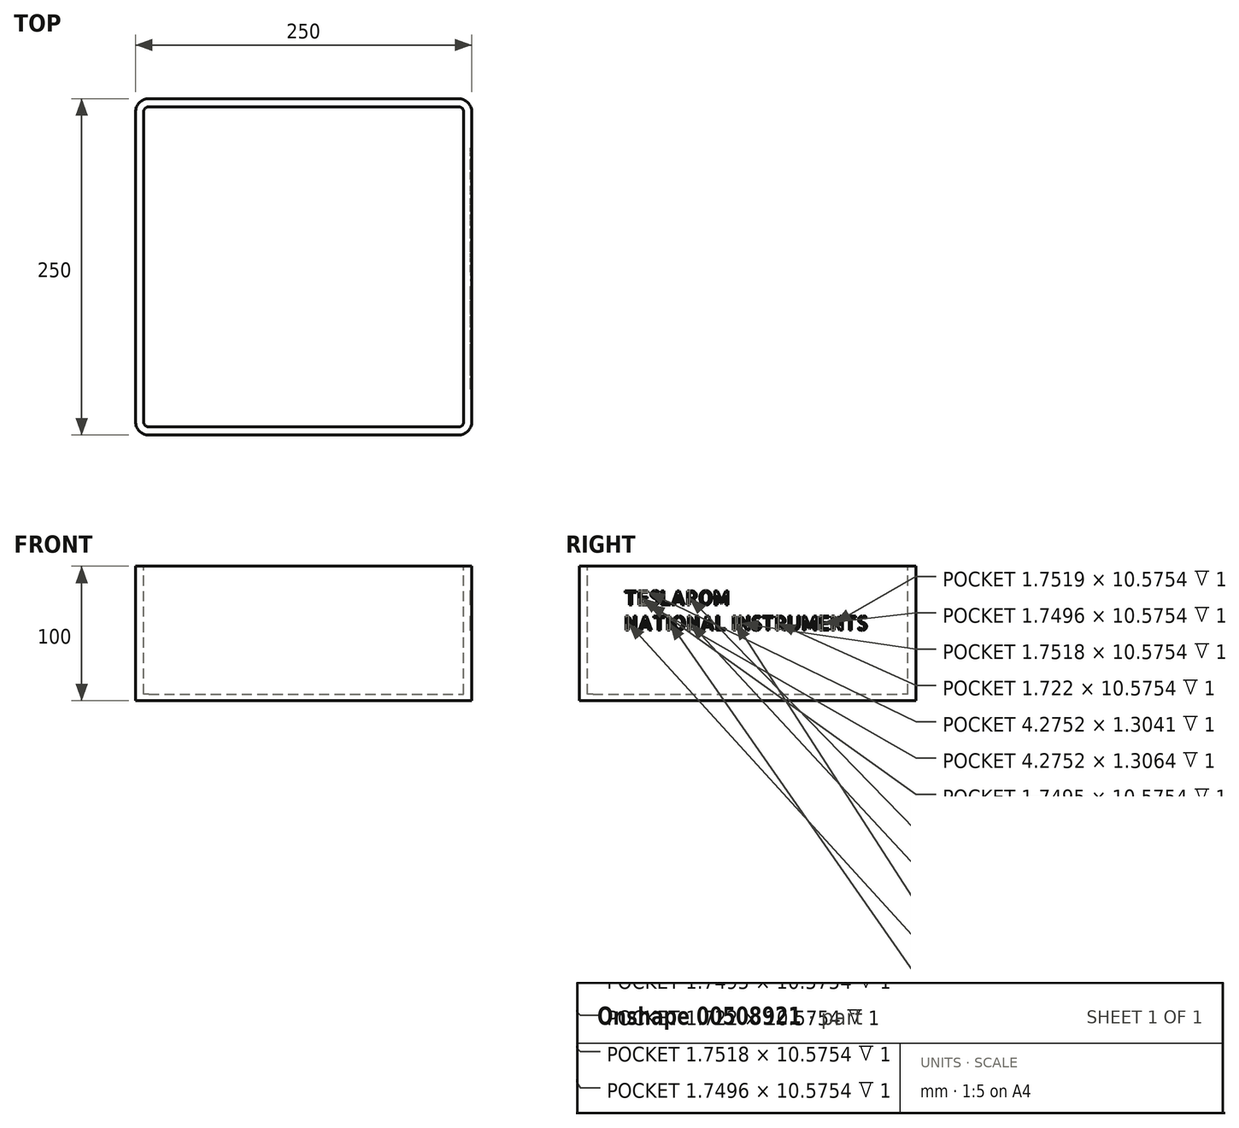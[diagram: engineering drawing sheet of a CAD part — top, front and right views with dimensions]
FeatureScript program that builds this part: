
annotation { "Feature Type Name" : "Feature", "Feature Type Description" : "" }
export const myFeature = defineFeature(function(context is Context, id is Id, definition is map)
    precondition{}
    {
        {
            var Q0;
            Q0=qCreatedBy(makeId("Top.planeOp"),FACE);
            var sketch = newSketch(context, id + "F0", { "sketchPlane" : qUnion([Q0])});
            skLineSegment(sketch, "E0.bottom", {"start": v(10, 0) * mm, "end": v(240, 0) * mm});
            skLineSegment(sketch, "E0.top", {"start": v(10, 250) * mm, "end": v(240, 250) * mm});
            skLineSegment(sketch, "E0.left", {"start": v(0, 10) * mm, "end": v(0, 240) * mm});
            skLineSegment(sketch, "E0.right", {"start": v(250, 10) * mm, "end": v(250, 240) * mm});
            skPoint(sketch, "E1.visualSharp", {"position": v(0, 250) * mm});
            skArc(sketch, "E1.filletArc", {"start": v(10, 250) * mm, "mid": v(2.93, 247.07) * mm, "end": v(0, 240) * mm});
            skPoint(sketch, "E2.visualSharp", {"position": v(250, 0) * mm});
            skArc(sketch, "E2.filletArc", {"start": v(240, 0) * mm, "mid": v(247.07, 2.93) * mm, "end": v(250, 10) * mm});
            skPoint(sketch, "E3.visualSharp", {"position": v(250, 250) * mm});
            skArc(sketch, "E3.filletArc", {"start": v(250, 240) * mm, "mid": v(247.07, 247.07) * mm, "end": v(240, 250) * mm});
            skPoint(sketch, "E4.visualSharp", {"position": v(0, 0) * mm});
            skArc(sketch, "E4.filletArc", {"start": v(0, 10) * mm, "mid": v(2.93, 2.93) * mm, "end": v(10, 0) * mm});
            skSolve(sketch);
        }
        {
            var Q0;
            Q0 = qSketchRegion(id + "F0", true);
            extrude(context, id + "F1", {"entities" : qUnion([Q0]), "depth" : 100 * mm});
        }
        {
            var Q0;
            Q0=makeQuery(id+"F1.opExtrude","CAP_FACE",FACE,{"disambiguationData":[OSD([sQuery(id+"F0.wireOp",EDGE,"E0.bottom"),sQuery(id+"F0.wireOp",EDGE,"E0.top"),sQuery(id+"F0.wireOp",EDGE,"E0.left"),sQuery(id+"F0.wireOp",EDGE,"E0.right"),sQuery(id+"F0.wireOp",EDGE,"E1.filletArc"),sQuery(id+"F0.wireOp",EDGE,"E2.filletArc"),sQuery(id+"F0.wireOp",EDGE,"E3.filletArc"),sQuery(id+"F0.wireOp",EDGE,"E4.filletArc")])],"isStart":false});
            var sketch = newSketch(context, id + "F2", { "sketchPlane" : qUnion([Q0])});
            skLineSegment(sketch, "E5.0", {"start": v(10, 244) * mm, "end": v(240, 244) * mm});
            skLineSegment(sketch, "E6.0", {"start": v(6, 10) * mm, "end": v(6, 240) * mm});
            skArc(sketch, "E7.0", {"start": v(10, 244) * mm, "mid": v(7.17, 242.83) * mm, "end": v(6, 240) * mm});
            skArc(sketch, "E8.0", {"start": v(244, 240) * mm, "mid": v(242.83, 242.83) * mm, "end": v(240, 244) * mm});
            skArc(sketch, "E8.1", {"start": v(6, 10) * mm, "mid": v(7.17, 7.17) * mm, "end": v(10, 6) * mm});
            skLineSegment(sketch, "E8.2", {"start": v(10, 6) * mm, "end": v(240, 6) * mm});
            skArc(sketch, "E8.3", {"start": v(240, 6) * mm, "mid": v(242.83, 7.17) * mm, "end": v(244, 10) * mm});
            skLineSegment(sketch, "E8.4", {"start": v(244, 10) * mm, "end": v(244, 240) * mm});
            skSolve(sketch);
        }
        {
            var Q0;
            Q0 = qSketchRegion(id + "F2", true);
            extrude(context, id + "F3", {"entities" : qUnion([Q0]), "operationType" : NewBodyOperationType.REMOVE, "oppositeDirection" : true, "depth" : 95 * mm});
        }
        {
            var Q0;
            Q0=makeQuery(id+"F1.opExtrude","SWEPT_FACE",FACE,{"disambiguationData":[OSD([sQuery(id+"F0.wireOp",EDGE,"E0.right")])]});
            var sketch = newSketch(context, id + "F4", { "sketchPlane" : qUnion([Q0])});
            skText(sketch, "E9", { "text": "TESLAROM\nNATIONAL INSTRUMENTS", "fontName": "AllertaStencil-Regular.ttf"});
            const initialGuessF4  = {"E9": [0.0333, 0.07116, 1, 0, 0.01058]};
            skSetInitialGuess(sketch, initialGuessF4);
            skSolve(sketch);
        }
        {
            var Q0;
            Q0 = qSketchRegion(id + "F4", true);
            extrude(context, id + "F5", {"entities" : qUnion([Q0]), "operationType" : NewBodyOperationType.REMOVE, "oppositeDirection" : true, "depth" : 1 * mm});
        }
    });
